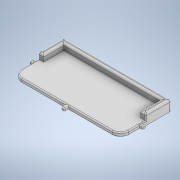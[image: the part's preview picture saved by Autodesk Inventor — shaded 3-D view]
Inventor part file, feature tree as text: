
AUTODESK INVENTOR PART (.ipt)
format: ipt  version: 2022.2 (Build 262287030, 287C)  size: 728,064 bytes
history: native  units: in
note: dims shown in document units (in); Inventor stores cm internally (conversion verified against a paired STEP export)
features: sketch x6, extrude x4, fillet x4, other x1, mirror x1, emboss x1
ambient origin geometry x8: Origin, YZ Plane, XZ Plane, XY Plane, X Axis, Y Axis, Z Axis, Center Point
bodies: Solid1 (feature_tree)
feature tree (17):
  other  "ledgeForKetchen"
  extrude  "Extrusion1"  Depth=6.375in
  extrude  "Extrusion3"  TaperAngle=0.0deg  [1 undecoded]
  extrude  "Extrusion4"  Depth=0.3in
  extrude  "Extrusion5"  Depth=0.25in
  mirror  "Mirror1"
  fillet  "Fillet1"  [1 undecoded]
  fillet  "Fillet2"  Radius=0.225in
  fillet  "Fillet3"  Radius=0.25in
  emboss  "Emboss1"
  sketch  "Sketch6"  dims[d16=0.1719in d17=0.0in d18=0.0625in d19=0.125in d20=0.0625in d21=0.3in d22=0.3in d23=1.25in d24=0.05in d25=0.0in d26=0.5in]
  fillet  "Fillet4"  [1 undecoded]
  sketch  "Sketch1"  dims[d0=3.0in d1=6.375in]
  sketch  "Sketch2"  dims[d2=0.25in d3=0.0in]
  sketch  "Sketch3"  dims[d4=0.3in d5=0.3in]
  sketch  "Sketch4"  dims[d6=0.3in d9=0.375in d10=0.0in d11=0.225in d12=0.25in d13=0.0in]
  sketch  "Sketch5"  dims[d15=0.25in]
note: 3 required parameter values undecoded (feature->parameter linkage not recoverable at this tier; creation-order binding heuristic only, values carry confidence <= 0.55)
